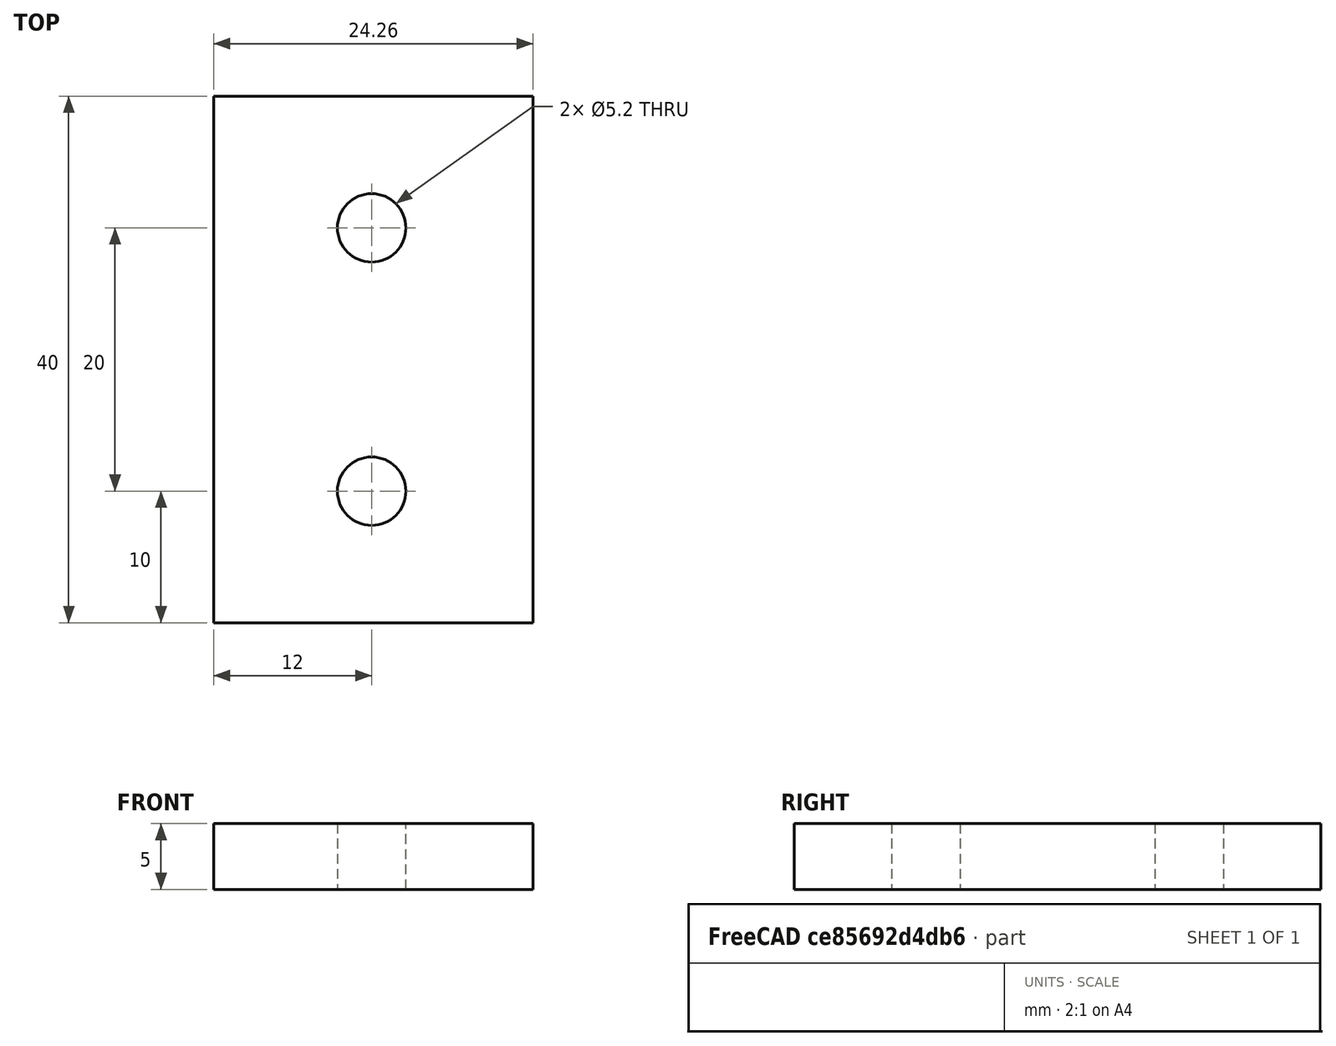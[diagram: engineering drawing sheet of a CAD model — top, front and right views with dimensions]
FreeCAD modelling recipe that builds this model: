
FCSTD DOCUMENT  (FreeCAD 0.20R29177 (Git))
Label: prostavka
License: All rights reserved
LicenseURL: http://en.wikipedia.org/wiki/All_rights_reserved
objects: Sketcher::SketchObject×1, PartDesign::Pad×1, PartDesign::Body×1
note: 4 computed .brp shape members not serialized (recipe doc carries the construction recipe); baked Part::Feature solids carry a one-line shape summary decoded from their .brp

FEATURE [Sketcher::SketchObject] Sketch
  FullyConstrained = false
  MapMode = 5
  Support = -> [XY_Plane]
  sketch-geometry (7):
    g0: Circle CenterX=12 CenterY=20 CenterZ=0 NormalX=0 NormalY=0 NormalZ=1 AngleXU=0 Radius=2.6
    g1: Circle CenterX=12 CenterY=-9e-16 CenterZ=0 NormalX=0 NormalY=0 NormalZ=1 AngleXU=0 Radius=2.6
    g2: LineSegment StartX=-5.50789 StartY=30 StartZ=0 EndX=41.3405 EndY=30 EndZ=0
    g3: LineSegment StartX=0 StartY=-10 StartZ=0 EndX=24.26 EndY=-10 EndZ=0
    g4: LineSegment StartX=0 StartY=-10 StartZ=0 EndX=0 EndY=30 EndZ=0
    g5: LineSegment StartX=24.26 StartY=-10 StartZ=0 EndX=24.26 EndY=30 EndZ=0
    g6: LineSegment StartX=0 StartY=30 StartZ=0 EndX=24.26 EndY=30 EndZ=0
  constraints (17):
    c: Diameter(g0) = 5.2
    c: Diameter(g1) = 5.2
    c: Distance(g1,g0) = 20
    c: Horizontal(g2)
    c: Distance(g2,g-1) = 30
    c: Block(g0)
    c: Horizontal(g3)
    c: Coincident(g4,g3)
    c: Vertical(g4)
    c: Coincident(g5,g3)
    c: Vertical(g5)
    c: Coincident(g6,g4)
    c: Coincident(g6,g5)
    c: Horizontal(g6)
    c: DistanceX(g3,g3) = 24.26
    c: Block(g3)
    c: DistanceY(g5,g5) = 40
FEATURE [PartDesign::Pad] Pad
  Direction = (0,0,1)
  Length = 5
  Length2 = 10
  Profile = -> Sketch
  ReferenceAxis = -> Sketch [N_Axis]
  Type = 0
FEATURE [PartDesign::Body] Body
  Group = -> [Sketch,Pad]
  Origin = -> Origin
  Tip = -> Pad
